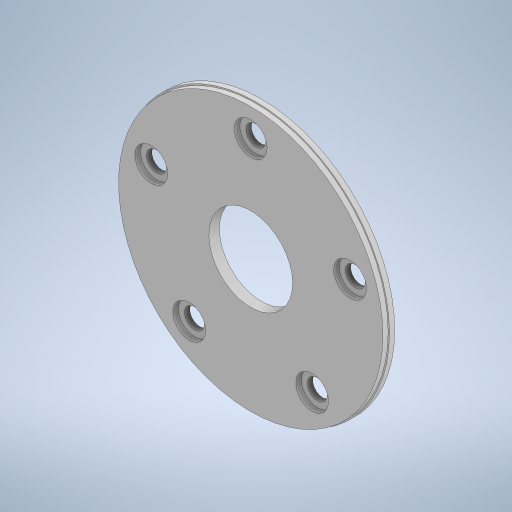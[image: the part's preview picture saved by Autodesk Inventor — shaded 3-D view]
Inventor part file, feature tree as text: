
AUTODESK INVENTOR PART (.ipt)
format: ipt  version: 2024 (Build 280153000, 153)  size: 274,944 bytes
history: native  units: in
note: dims shown in document units (in); Inventor stores cm internally (conversion verified against a paired STEP export)
features: extrude x2, sketch x2
ambient origin geometry x8: Origin, YZ Plane, XZ Plane, XY Plane, X Axis, Y Axis, Z Axis, Center Point
bodies: Solid1 (feature_tree)
feature tree (4):
  extrude  "Extrusion1"  Depth=5.1in
  extrude  "Extrusion2"  Depth=0.1in TaperAngle=360.0deg
  sketch  "Sketch1"  dims[d0=1.6in d1=5.1in]
  sketch  "Sketch2"  dims[d2=1.997in d3=1.9685in d5=360.0deg d7=0.1in d8=0.0in d9=0.626in d10=1.9685in d12=360.0deg d14=0.1in d15=0.0in]
